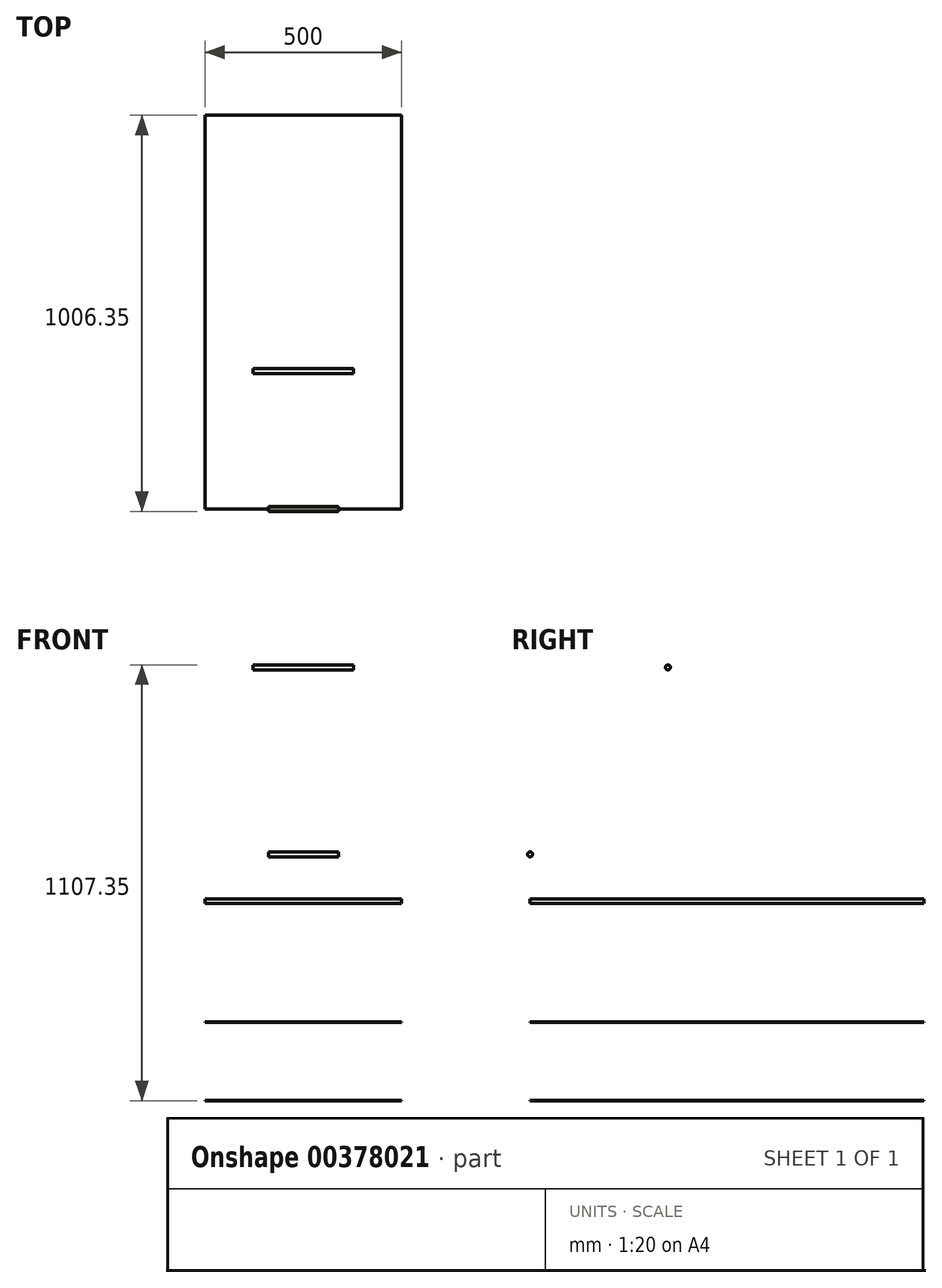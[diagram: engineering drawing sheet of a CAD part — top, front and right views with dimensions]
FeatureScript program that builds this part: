
annotation { "Feature Type Name" : "Feature", "Feature Type Description" : "" }
export const myFeature = defineFeature(function(context is Context, id is Id, definition is map)
    precondition{}
    {
        {
            var Q0;
            Q0=qCreatedBy(makeId("Right.planeOp"),FACE);
            var sketch = newSketch(context, id + "F0", { "sketchPlane" : qUnion([Q0])});
            skCircle(sketch, "E0", {"center": v(0, 0) * mm, "radius": 6.35 * mm});
            skSolve(sketch);
        }
        {
            var Q0;
            Q0 = qSketchRegion(id + "F0", true);
            extrude(context, id + "F1", {"entities" : qUnion([Q0]), "endBound" : BoundingType.SYMMETRIC, "depth" : 177.8 * mm});
        }
        {
            var Q0;
            Q0=qCreatedBy(makeId("Right.planeOp"),FACE);
            var sketch = newSketch(context, id + "F2", { "sketchPlane" : qUnion([Q0])});
            skPoint(sketch, "E1.0", {"position": v(0, 0) * mm});
            skLineSegment(sketch, "E2.bottom", {"start": v(0, -114) * mm, "end": v(1000, -114) * mm});
            skLineSegment(sketch, "E2.top", {"start": v(0, -125) * mm, "end": v(1000, -125) * mm});
            skLineSegment(sketch, "E2.left", {"start": v(0, -114) * mm, "end": v(0, -125) * mm});
            skLineSegment(sketch, "E2.right", {"start": v(1000, -114) * mm, "end": v(1000, -125) * mm});
            skLineSegment(sketch, "E3.bottom", {"start": v(0, -427) * mm, "end": v(1000, -427) * mm});
            skLineSegment(sketch, "E3.top", {"start": v(0, -426) * mm, "end": v(1000, -426) * mm});
            skLineSegment(sketch, "E3.left", {"start": v(0, -427) * mm, "end": v(0, -426) * mm});
            skLineSegment(sketch, "E3.right", {"start": v(1000, -427) * mm, "end": v(1000, -426) * mm});
            skLineSegment(sketch, "E4.bottom", {"start": v(0, -626) * mm, "end": v(1000, -626) * mm});
            skLineSegment(sketch, "E4.top", {"start": v(0, -625) * mm, "end": v(1000, -625) * mm});
            skLineSegment(sketch, "E4.left", {"start": v(0, -626) * mm, "end": v(0, -625) * mm});
            skLineSegment(sketch, "E4.right", {"start": v(1000, -626) * mm, "end": v(1000, -625) * mm});
            skSolve(sketch);
        }
        {
            var Q0;
            Q0 = qSketchRegion(id + "F2", true);
            extrude(context, id + "F3", {"entities" : qUnion([Q0]), "endBound" : BoundingType.SYMMETRIC, "depth" : 500 * mm});
        }
        {
            var Q0;
            Q0=qCreatedBy(makeId("Right.planeOp"),FACE);
            var sketch = newSketch(context, id + "F4", { "sketchPlane" : qUnion([Q0])});
            skCircle(sketch, "E5", {"center": v(350, 475) * mm, "radius": 6.35 * mm});
            skSolve(sketch);
        }
        {
            var Q0;
            Q0 = qSketchRegion(id + "F4", true);
            extrude(context, id + "F5", {"entities" : qUnion([Q0]), "endBound" : BoundingType.SYMMETRIC, "depth" : 254 * mm});
        }
    });
